# Revit family: Elevator_Accessories_Garaventa_UPS-Shelf
name_source: partatom
category: Generic Models
units: mm (PartAtom-declared; Revit-internal decimal feet)

## family parameters
Always vertical = No
Can host rebar = No
Classification Number = 23.50.05.11.24.14
Cut with Voids When Loaded = No
Maintain Annotation Orientation = No
Part Type = Normal
Room Calculation Point = No
Round Connector Dimension = Use Diameter
Shared = No
Work Plane-Based = Yes

## types (1)
- as Specified
    Assembly Code = D1010
    Construction Details = http://www.arcat.com
    Default Elevation = 0' - 0"
    Description = Garaventa Lift UPS with Shelf
    Expected Lifespan (Years) = 0
    Green Building-LEED = http://www.arcat.com
    Keynote = 14 20 00
    Maintenance Schedule (Months) = 0
    Manufacturer = Garaventa Lift
    Manufacturer Fax = 604-594-9915
    Manufacturer Website = http://www.garaventalift.com
    Model = UPS with Shelf
    Product Data = http://www.arcat.com
    Revision = R1_2017-06
    Sales Information = http://www.garaventalift.com
    SpecWizard = http://www.arcat.com
    Specification = http://www.arcat.com
    URL = http://www.garaventalift.com
    Unit Depth = 0' - 5"
    Unit Height = 0' - 9"
    Unit Width = 1' - 8"
    Warranty Duration (Years) = 0

## geometry (parser evidence)
native form markers: Sweep x2
no freeform markers — native parametric forms only
